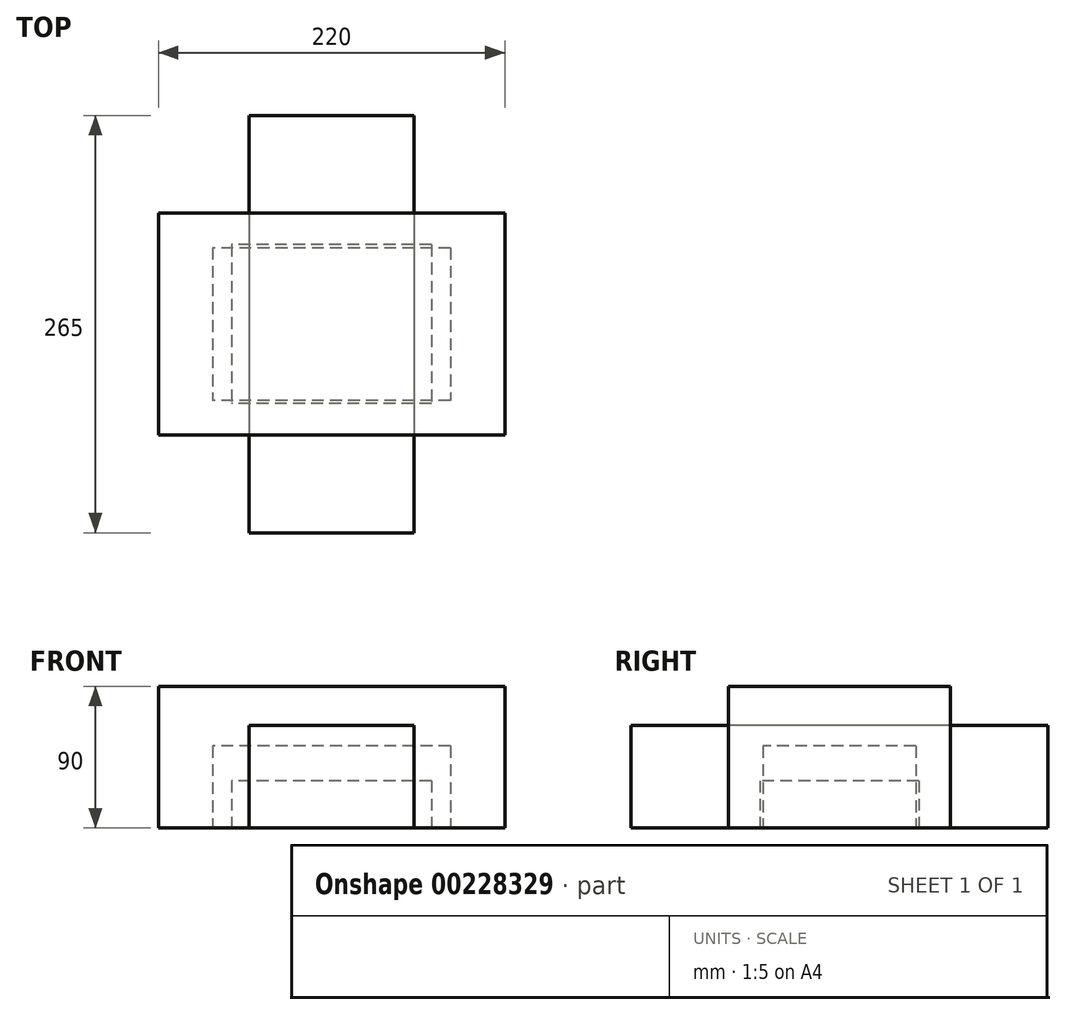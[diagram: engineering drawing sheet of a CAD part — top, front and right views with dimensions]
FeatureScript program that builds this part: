
annotation { "Feature Type Name" : "Feature", "Feature Type Description" : "" }
export const myFeature = defineFeature(function(context is Context, id is Id, definition is map)
    precondition{}
    {
        {
            var Q0;
            Q0=qCreatedBy(makeId("Top.planeOp"),FACE);
            var sketch = newSketch(context, id + "F0", { "sketchPlane" : qUnion([Q0])});
            skLineSegment(sketch, "E0.bottom", {"start": v(52.5, 132.5) * mm, "end": v(-52.5, 132.5) * mm});
            skLineSegment(sketch, "E0.top", {"start": v(52.5, -132.5) * mm, "end": v(-52.5, -132.5) * mm});
            skLineSegment(sketch, "E0.left", {"start": v(52.5, 132.5) * mm, "end": v(52.5, -132.5) * mm});
            skLineSegment(sketch, "E0.right", {"start": v(-52.5, 132.5) * mm, "end": v(-52.5, -132.5) * mm});
            skPoint(sketch, "E0.middle", {"position": v(0, 0) * mm});
            skSolve(sketch);
        }
        {
            var Q0;
            Q0=makeQuery(id+"F0.imprint","IMPRINT",FACE,{"disambiguationData":[TD([[makeQuery(id+"F0.imprint","IMPRINT",EDGE,{"derivedFrom":sQuery(id+"F0.wireOp",EDGE,"E0.bottom")}),1.0]])]});
            extrude(context, id + "F1", {"entities" : qUnion([Q0]), "depth" : 65 * mm});
        }
        {
            var Q0;
            Q0=qCreatedBy(makeId("Top.planeOp"),FACE);
            var sketch = newSketch(context, id + "F2", { "sketchPlane" : qUnion([Q0])});
            skLineSegment(sketch, "E1.bottom", {"start": v(75.5, 48.5) * mm, "end": v(-75.5, 48.5) * mm});
            skLineSegment(sketch, "E1.top", {"start": v(75.5, -48.5) * mm, "end": v(-75.5, -48.5) * mm});
            skLineSegment(sketch, "E1.left", {"start": v(75.5, 48.5) * mm, "end": v(75.5, -48.5) * mm});
            skLineSegment(sketch, "E1.right", {"start": v(-75.5, 48.5) * mm, "end": v(-75.5, -48.5) * mm});
            skPoint(sketch, "E1.middle", {"position": v(0, 0) * mm});
            skSolve(sketch);
        }
        {
            var Q0;
            Q0=makeQuery(id+"F2.imprint","IMPRINT",FACE,{"disambiguationData":[TD([[makeQuery(id+"F2.imprint","IMPRINT",EDGE,{"derivedFrom":sQuery(id+"F2.wireOp",EDGE,"E1.bottom")}),1.0]])]});
            extrude(context, id + "F3", {"entities" : qUnion([Q0]), "depth" : 52 * mm});
        }
        {
            var Q0;
            Q0=qCreatedBy(makeId("Top.planeOp"),FACE);
            var sketch = newSketch(context, id + "F4", { "sketchPlane" : qUnion([Q0])});
            skLineSegment(sketch, "E2.bottom", {"start": v(110, 70.5) * mm, "end": v(-110, 70.5) * mm});
            skLineSegment(sketch, "E2.top", {"start": v(110, -70.5) * mm, "end": v(-110, -70.5) * mm});
            skLineSegment(sketch, "E2.left", {"start": v(110, 70.5) * mm, "end": v(110, -70.5) * mm});
            skLineSegment(sketch, "E2.right", {"start": v(-110, 70.5) * mm, "end": v(-110, -70.5) * mm});
            skPoint(sketch, "E2.middle", {"position": v(0, 0) * mm});
            skSolve(sketch);
        }
        {
            var Q0;
            Q0=makeQuery(id+"F4.imprint","IMPRINT",FACE,{"disambiguationData":[TD([[makeQuery(id+"F4.imprint","IMPRINT",EDGE,{"derivedFrom":sQuery(id+"F4.wireOp",EDGE,"E2.bottom")}),1.0]])]});
            extrude(context, id + "F5", {"entities" : qUnion([Q0]), "depth" : 90 * mm});
        }
        {
            var Q0;
            Q0=qCreatedBy(makeId("Top.planeOp"),FACE);
            var sketch = newSketch(context, id + "F6", { "sketchPlane" : qUnion([Q0])});
            skLineSegment(sketch, "E3.bottom", {"start": v(63.5, 50.5) * mm, "end": v(-63.5, 50.5) * mm});
            skLineSegment(sketch, "E3.top", {"start": v(63.5, -50.5) * mm, "end": v(-63.5, -50.5) * mm});
            skLineSegment(sketch, "E3.left", {"start": v(63.5, 50.5) * mm, "end": v(63.5, -50.5) * mm});
            skLineSegment(sketch, "E3.right", {"start": v(-63.5, 50.5) * mm, "end": v(-63.5, -50.5) * mm});
            skPoint(sketch, "E3.middle", {"position": v(0, 0) * mm});
            skSolve(sketch);
        }
        {
            var Q0;
            Q0=makeQuery(id+"F6.imprint","IMPRINT",FACE,{"disambiguationData":[TD([[makeQuery(id+"F6.imprint","IMPRINT",EDGE,{"derivedFrom":sQuery(id+"F6.wireOp",EDGE,"E3.bottom")}),1.0]])]});
            extrude(context, id + "F7", {"entities" : qUnion([Q0]), "depth" : 30 * mm});
        }
    });
